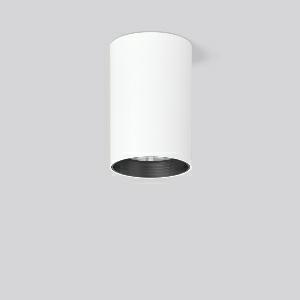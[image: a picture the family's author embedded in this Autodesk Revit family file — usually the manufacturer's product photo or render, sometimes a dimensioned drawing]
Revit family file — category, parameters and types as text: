
# Revit family: heledon_maxi_a_931243_002_76_d496
name_source: partatom
category: Lighting Fixtures
units: mm (PartAtom-declared; Revit-internal decimal feet)

## family parameters
Cut with Voids When Loaded = No
Host = Face
Light Source = No
Part Type = Normal
Room Calculation Point = No
Round Connector Dimension = Use Diameter
Shared = No

## types (1)
- HELEDON maxi A (1 x LED Modul 920 meat+, 1900 lm, 2000)
    Apparent Load = 33 VA
    Approval mark = CE
    CIE Flux Codes = 96 99 100 100 100
    Color Rendering = 90
    Color Temperature = 2000
    Default Elevation = 1800 mm
    Description = Series: HELEDON maxi
Cylindrical surface-mounted downlight. Housing: die-cast aluminium, powder-coated. Internal ceiling frame polycarbonate with bayonet mounting. Black plastic ring and recessed LED to prevent glare from the side. Optical assembly with lens made of plastic (polycarbonate) for the best homogeneous light distribution - can be changed without tools. Special LED for illumination of meat included. Suitable for Ceiling mounting. Easy installation with a separate ceiling frame with bayonet mounting and plug connection. Driver integrated. Connected via plug-in connector. High quality converter without flickering and stroboscopic effect. The following accessories can be mounted without use of tools: interchangeable lenses, decorative glasses, honeycomb louvre, clear and frosted diffusers, white interchangeable plastic ring. 
Colour: traffic white, matt (RAL 9016)
Diameter: 123 mm
Height: 183 mm
Lamp: LED
Socket: without socket
Colour temperature: meat +
System power: 33 W
Rated luminous flux: 1900 lm
Luminous efficiency: 58 lm/W
Control gear: Converter, dimmable, DALI
Protection class: I
Type of protection: IP 20
    Height = 183 mm
    Lamp = 1 x LED Modul 920 meat+
    Lamp Light Flux = 1900 lm
    Lamp count = 1
    Length = 123 mm
    Lifetime = 50000 h
    Luminous efficacy = 58 lm/W
    Manufacturer = RZB
    ModVariant = No
    Model = 931243.002.76
    Mounting Place = Ceiling
    Mounting Type = Surface mounted
    Number of Poles = 1
    OnlyDefault = Yes
    Power Factor = 1
    Product Name = HELEDON maxi A
    Product group = Surface mounted downlights
    ProductGroupID = 302
    Protection Class = Protection class I
    Protection Degree = IP 20
    RLX_Detail_Level = 1
    RLX_Emergency_Light_Flux = 0 lm
    RLX_Emergency_Type = 0
    RLX_Emergency_Type_DB = No
    RlxData = <blob elided: 96729 chars, md5=40f346be>
    Socket = socket
    Standby Power = 0 W
    System Light Flux = 1900 lm
    System Power = 33 W
    Type Comments = Product without accessories
    Type Image = 931193.002.jpg
    URL = http://relux.com
    VarID = ---
    Voltage = 230 V
    Voltage Range = 220-240 V
    Weight = 0.00 kg
    Width = 0 mm  [stored 0 ft]

note: [stored X ft] marks values corroborated as IEEE doubles in the binary element streams (Revit-internal decimal feet)

## geometry (parser evidence)
native form markers: Blend x4, Sweep x10
no freeform markers — native parametric forms only
